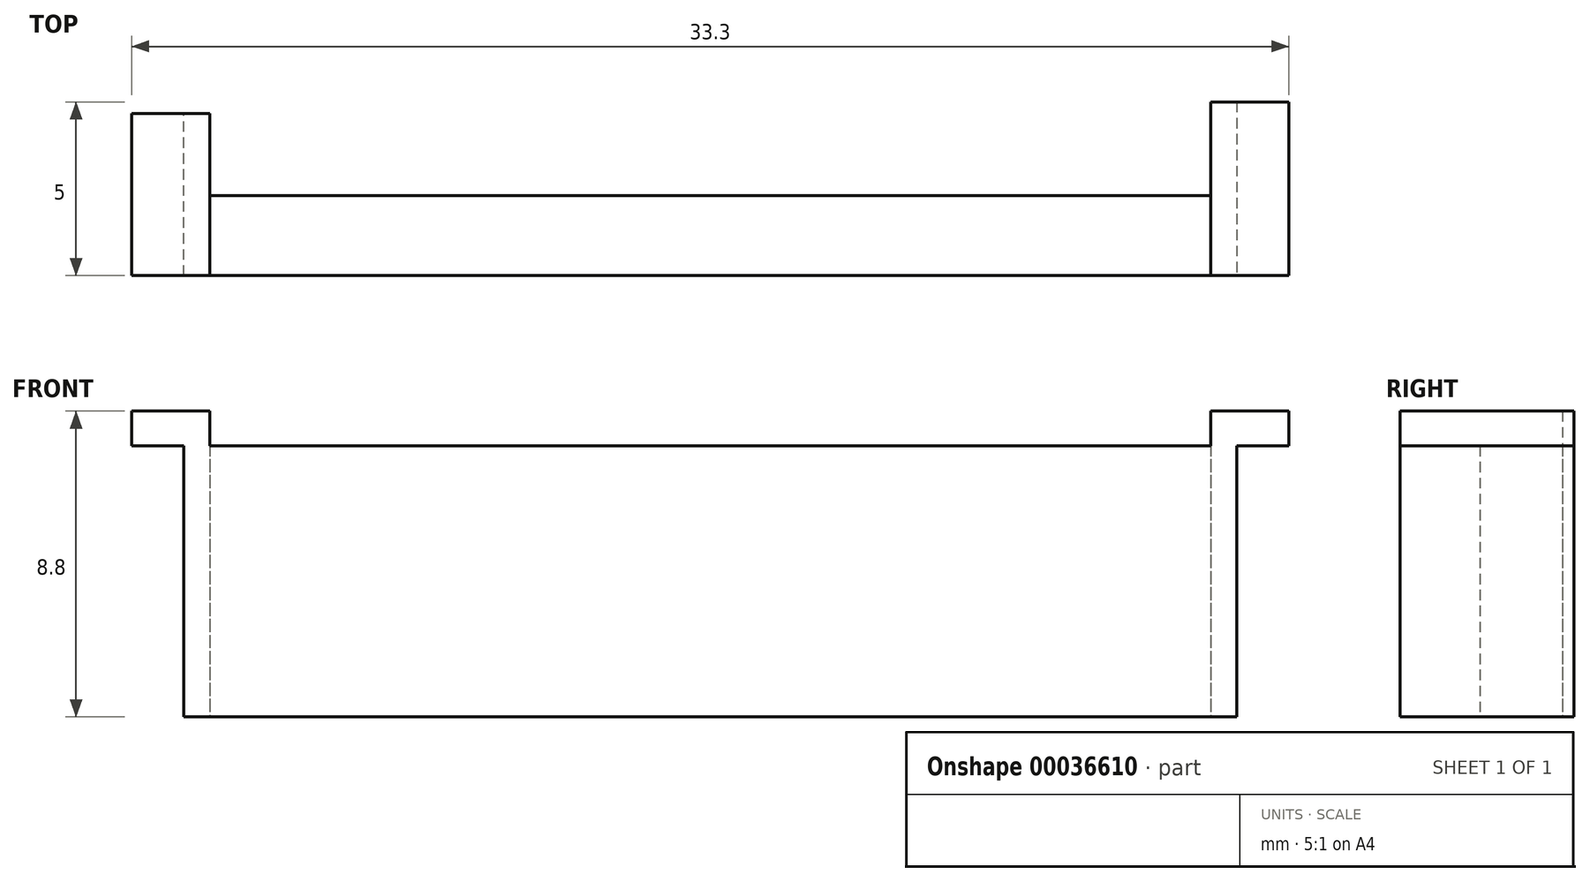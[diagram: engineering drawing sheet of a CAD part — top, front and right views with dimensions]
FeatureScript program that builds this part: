
annotation { "Feature Type Name" : "Feature", "Feature Type Description" : "" }
export const myFeature = defineFeature(function(context is Context, id is Id, definition is map)
    precondition{}
    {
        {
            var Q0;
            Q0=qCreatedBy(makeId("Top.planeOp"),FACE);
            var sketch = newSketch(context, id + "F0", { "sketchPlane" : qUnion([Q0])});
            skLineSegment(sketch, "E0", {"start": v(-18.3, 0) * mm, "end": v(-18.3, 4.67) * mm});
            skLineSegment(sketch, "E1", {"start": v(-18.3, 4.67) * mm, "end": v(-17.55, 4.67) * mm});
            skLineSegment(sketch, "E2", {"start": v(-17.55, 4.67) * mm, "end": v(-17.55, 2.3) * mm});
            skLineSegment(sketch, "E3", {"start": v(-17.55, 2.3) * mm, "end": v(11.25, 2.3) * mm});
            skLineSegment(sketch, "E4", {"start": v(11.25, 2.3) * mm, "end": v(11.25, 5) * mm});
            skLineSegment(sketch, "E5", {"start": v(11.25, 5) * mm, "end": v(12, 5) * mm});
            skLineSegment(sketch, "E6", {"start": v(12, 5) * mm, "end": v(12, 0) * mm});
            skLineSegment(sketch, "E7", {"start": v(12, 0) * mm, "end": v(-18.3, 0) * mm});
            skSolve(sketch);
        }
        {
            var Q0;
            Q0 = qSketchRegion(id + "F0", true);
            extrude(context, id + "F1", {"entities" : qUnion([Q0]), "depth" : 7.8 * mm});
        }
        {
            var Q0;
            Q0=makeQuery(id+"F1.opExtrude","CAP_FACE",FACE,{"disambiguationData":[OSD([sQuery(id+"F0.wireOp",EDGE,"E0"),sQuery(id+"F0.wireOp",EDGE,"E1"),sQuery(id+"F0.wireOp",EDGE,"E2"),sQuery(id+"F0.wireOp",EDGE,"E3"),sQuery(id+"F0.wireOp",EDGE,"E4"),sQuery(id+"F0.wireOp",EDGE,"E5"),sQuery(id+"F0.wireOp",EDGE,"E6"),sQuery(id+"F0.wireOp",EDGE,"E7")])],"isStart":false});
            var sketch = newSketch(context, id + "F2", { "sketchPlane" : qUnion([Q0])});
            skLineSegment(sketch, "E8", {"start": v(-17.55, 4.67) * mm, "end": v(-17.55, 2.3) * mm});
            skLineSegment(sketch, "E9", {"start": v(-17.55, 2.3) * mm, "end": v(11.25, 2.3) * mm});
            skLineSegment(sketch, "E10", {"start": v(11.25, 2.3) * mm, "end": v(11.25, 5) * mm});
            skLineSegment(sketch, "E11", {"start": v(11.25, 5) * mm, "end": v(13.5, 5) * mm});
            skLineSegment(sketch, "E12", {"start": v(13.5, 5) * mm, "end": v(13.5, 0) * mm});
            skLineSegment(sketch, "E13", {"start": v(13.5, 0) * mm, "end": v(-19.8, 0) * mm});
            skLineSegment(sketch, "E14", {"start": v(-19.8, 0) * mm, "end": v(-19.8, 4.67) * mm});
            skLineSegment(sketch, "E15", {"start": v(-19.8, 4.67) * mm, "end": v(-17.55, 4.67) * mm});
            skSolve(sketch);
        }
        {
            var Q0;
            Q0 = qSketchRegion(id + "F2", true);
            extrude(context, id + "F3", {"entities" : qUnion([Q0]), "operationType" : NewBodyOperationType.ADD, "depth" : 1 * mm});
        }
        {
            var Q0;
            Q0=makeQuery(id+"F3.boolean.opBoolean","MERGE",FACE,{"derivedFrom":[makeQuery(id+"F1.opExtrude","SWEPT_FACE",FACE,{"disambiguationData":[OSD([sQuery(id+"F0.wireOp",EDGE,"E7")])]}),makeQuery(id+"F3.opExtrude","SWEPT_FACE",FACE,{"disambiguationData":[OSD([sQuery(id+"F2.wireOp",EDGE,"E13")])]})]});
            var sketch = newSketch(context, id + "F4", { "sketchPlane" : qUnion([Q0])});
            skLineSegment(sketch, "E16", {"start": v(-17.55, 8.8) * mm, "end": v(-17.55, 7.8) * mm});
            skLineSegment(sketch, "E17", {"start": v(-17.55, 7.8) * mm, "end": v(11.25, 7.8) * mm});
            skLineSegment(sketch, "E18", {"start": v(11.25, 7.8) * mm, "end": v(11.25, 8.8) * mm});
            skLineSegment(sketch, "E19", {"start": v(11.25, 8.8) * mm, "end": v(-17.55, 8.8) * mm});
            skSolve(sketch);
        }
        {
            var Q0;
            Q0 = qSketchRegion(id + "F4", true);
            extrude(context, id + "F5", {"entities" : qUnion([Q0]), "operationType" : NewBodyOperationType.REMOVE, "endBound" : BoundingType.THROUGH_ALL, "oppositeDirection" : true, "depth" : 25 * mm});
        }
    });
